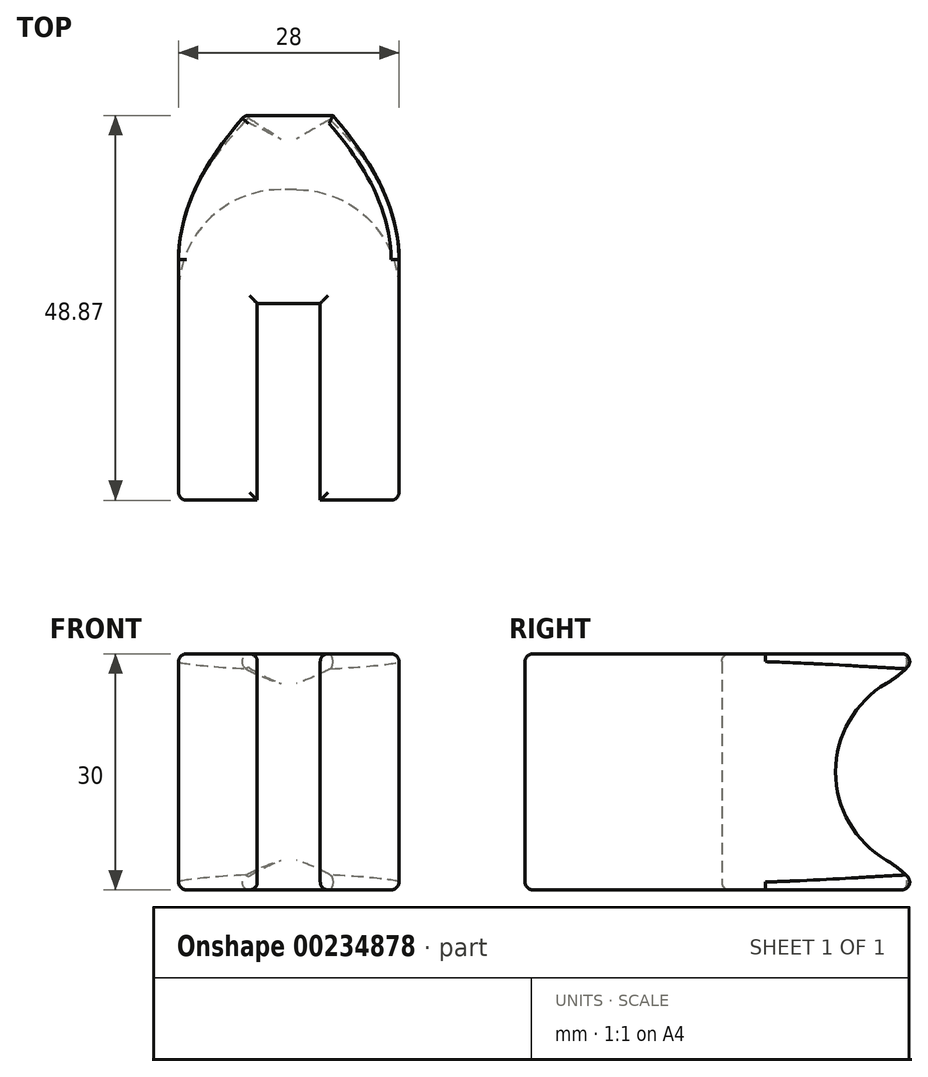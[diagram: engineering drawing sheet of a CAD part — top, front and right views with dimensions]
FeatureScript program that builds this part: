
annotation { "Feature Type Name" : "Feature", "Feature Type Description" : "" }
export const myFeature = defineFeature(function(context is Context, id is Id, definition is map)
    precondition{}
    {
        {
            var Q0;
            Q0=qCreatedBy(makeId("Top.planeOp"),FACE);
            var sketch = newSketch(context, id + "F0", { "sketchPlane" : qUnion([Q0])});
            skLineSegment(sketch, "E0", {"start": v(-15.63, 24.87) * mm, "end": v(12.37, 24.87) * mm});
            skLineSegment(sketch, "E1", {"start": v(-15.63, 24.87) * mm, "end": v(-15.63, -25.13) * mm});
            skLineSegment(sketch, "E2", {"start": v(-15.63, -25.13) * mm, "end": v(-5.63, -25.13) * mm});
            skLineSegment(sketch, "E3", {"start": v(-5.63, -25.13) * mm, "end": v(-5.63, -0.13) * mm});
            skLineSegment(sketch, "E4", {"start": v(-5.63, -0.13) * mm, "end": v(2.37, -0.13) * mm});
            skLineSegment(sketch, "E5", {"start": v(2.37, -0.13) * mm, "end": v(2.37, -25.13) * mm});
            skLineSegment(sketch, "E6", {"start": v(2.37, -25.13) * mm, "end": v(12.37, -25.13) * mm});
            skLineSegment(sketch, "E7", {"start": v(12.37, 24.87) * mm, "end": v(12.37, -25.13) * mm});
            skSolve(sketch);
        }
        {
            var Q0;
            Q0 = qSketchRegion(id + "F0", true);
            extrude(context, id + "F1", {"entities" : qUnion([Q0]), "depth" : 30 * mm});
        }
        {
            var Q0;
            Q0=qCreatedBy(makeId("Right.planeOp"),FACE);
            var sketch = newSketch(context, id + "F2", { "sketchPlane" : qUnion([Q0])});
            skLineSegment(sketch, "E8", {"start": v(27.34, 0) * mm, "end": v(27.34, 15) * mm, "construction": true});
            skCircle(sketch, "E9", {"center": v(27.34, 15) * mm, "radius": 13 * mm});
            skSolve(sketch);
        }
        {
            var Q0;
            Q0=makeQuery(id+"F2.imprint","IMPRINT",FACE,{"disambiguationData":[TD([[makeQuery(id+"F2.imprint","IMPRINT",EDGE,{"derivedFrom":sQuery(id+"F2.wireOp",EDGE,"E9")}),1.0]])]});
            var Q1;
            Q1=sQuery(id+"F2.wireOp",EDGE,"E9");
            extrude(context, id + "F3", {"entities" : qUnion([Q0]), "surfaceEntities" : qUnion([Q1]), "endBound" : BoundingType.SYMMETRIC, "depth" : 50 * mm, "hasSecondDirection" : true, "secondDirectionOppositeDirection" : true, "secondDirectionDepth" : 25 * mm});
        }
        {
            var Q0;
            Q0=makeQuery(id+"F3.opExtrude","SWEPT_BODY",BODY,{"disambiguationData":[OSD([sQuery(id+"F2.wireOp",EDGE,"E9")])]});
            var Q1;
            Q1=makeQuery(id+"F1.opExtrude","SWEPT_BODY",BODY,{"disambiguationData":[OSD([sQuery(id+"F0.wireOp",EDGE,"E0"),sQuery(id+"F0.wireOp",EDGE,"E1"),sQuery(id+"F0.wireOp",EDGE,"E2"),sQuery(id+"F0.wireOp",EDGE,"E3"),sQuery(id+"F0.wireOp",EDGE,"E4"),sQuery(id+"F0.wireOp",EDGE,"E5"),sQuery(id+"F0.wireOp",EDGE,"E6"),sQuery(id+"F0.wireOp",EDGE,"E7")])]});
            booleanBodies(context, id + "F4", {"operationType" : BooleanOperationType.SUBTRACTION, "tools" : qUnion([Q0]), "targets" : qUnion([Q1])});
        }
        {
            var Q0;
            Q0=makeQuery(id+"F4.opBoolean","COPY",FACE,{"derivedFrom":makeQuery(id+"F3.opExtrude","SWEPT_FACE",FACE,{"disambiguationData":[OSD([sQuery(id+"F2.wireOp",EDGE,"E9")])]})});
            fillet(context, id + "F5", {"entities" : qUnion([Q0]), "radius" : 13 * mm, "tangentPropagation" : true, "allowEdgeOverflow" : false});
        }
        {
            var Q0;
            Q0=makeQuery(id+"F1.opExtrude","CAP_FACE",FACE,{"disambiguationData":[OSD([sQuery(id+"F0.wireOp",EDGE,"E0"),sQuery(id+"F0.wireOp",EDGE,"E1"),sQuery(id+"F0.wireOp",EDGE,"E2"),sQuery(id+"F0.wireOp",EDGE,"E3"),sQuery(id+"F0.wireOp",EDGE,"E4"),sQuery(id+"F0.wireOp",EDGE,"E5"),sQuery(id+"F0.wireOp",EDGE,"E6"),sQuery(id+"F0.wireOp",EDGE,"E7")])],"isStart":true});
            var Q1;
            Q1=makeQuery(id+"F5.opFillet","BLEND_FACE",FACE,{"disambiguationData":[OSD([sQuery(id+"F0.wireOp",EDGE,"E1"),sQuery(id+"F2.wireOp",EDGE,"E9")])]});
            var Q2;
            Q2=makeQuery(id+"F1.opExtrude","CAP_FACE",FACE,{"disambiguationData":[OSD([sQuery(id+"F0.wireOp",EDGE,"E0"),sQuery(id+"F0.wireOp",EDGE,"E1"),sQuery(id+"F0.wireOp",EDGE,"E2"),sQuery(id+"F0.wireOp",EDGE,"E3"),sQuery(id+"F0.wireOp",EDGE,"E4"),sQuery(id+"F0.wireOp",EDGE,"E5"),sQuery(id+"F0.wireOp",EDGE,"E6"),sQuery(id+"F0.wireOp",EDGE,"E7")])],"isStart":false});
            var Q3;
            Q3=makeQuery(id+"F1.opExtrude","SWEPT_FACE",FACE,{"disambiguationData":[OSD([sQuery(id+"F0.wireOp",EDGE,"E1")])]});
            var Q4;
            Q4=makeQuery(id+"F1.opExtrude","SWEPT_FACE",FACE,{"disambiguationData":[OSD([sQuery(id+"F0.wireOp",EDGE,"E7")])]});
            fillet(context, id + "F6", {"entities" : qUnion([Q0, Q1, Q2, Q3, Q4]), "radius" : 1 * mm, "tangentPropagation" : true, "allowEdgeOverflow" : false});
        }
    });
